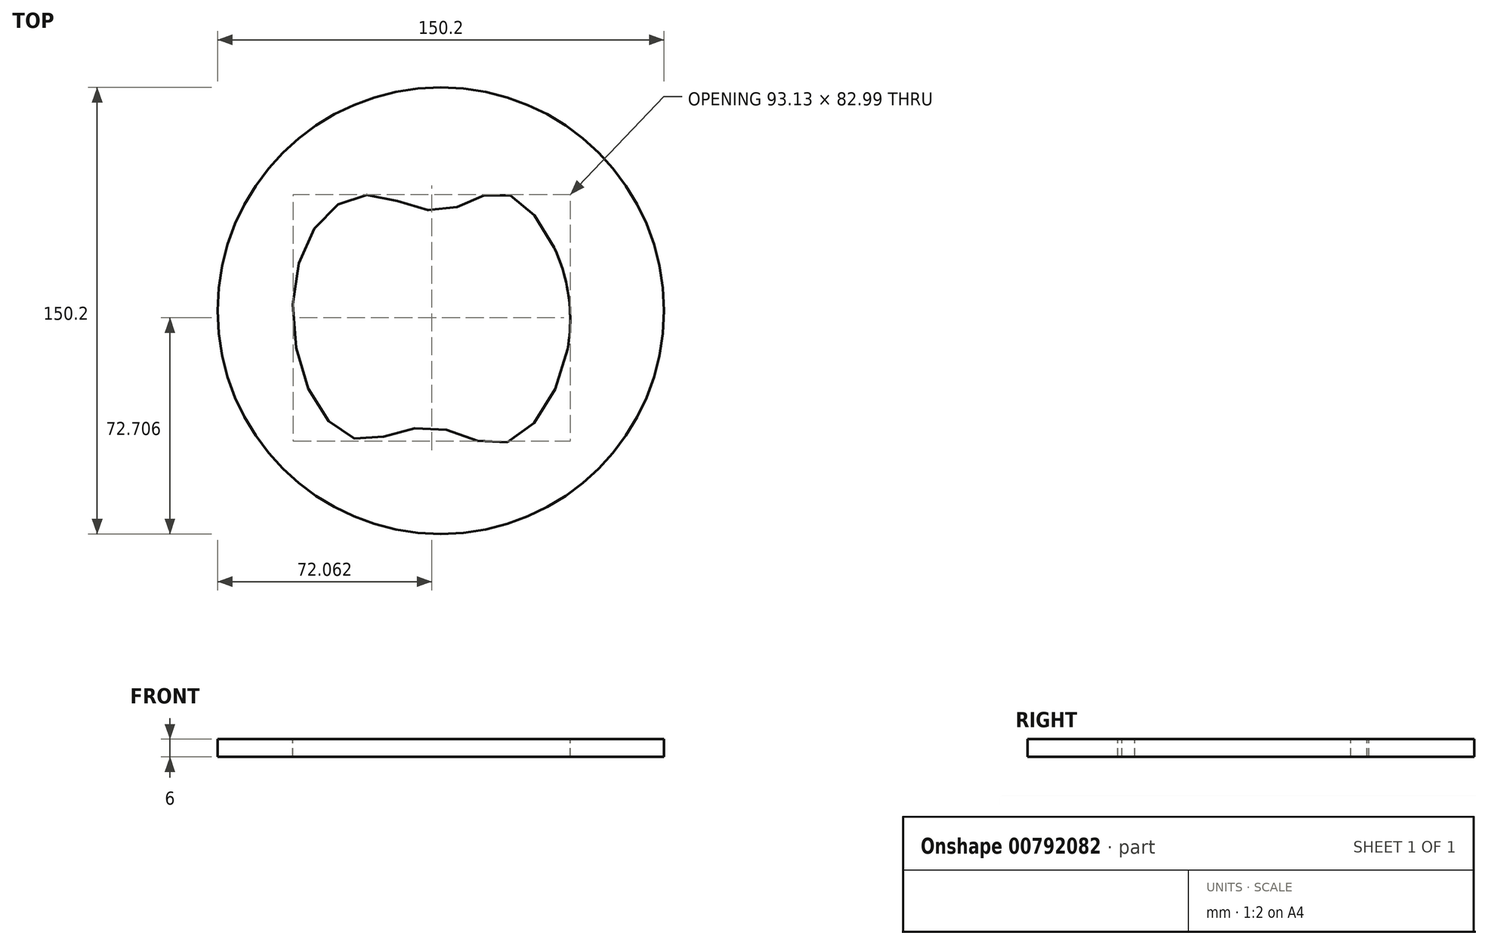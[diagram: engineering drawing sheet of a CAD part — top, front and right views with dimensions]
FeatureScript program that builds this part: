
annotation { "Feature Type Name" : "Feature", "Feature Type Description" : "" }
export const myFeature = defineFeature(function(context is Context, id is Id, definition is map)
    precondition{}
    {
        {
            var Q0;
            Q0=qCreatedBy(makeId("Top.planeOp"),FACE);
            var sketch = newSketch(context, id + "F0", { "sketchPlane" : qUnion([Q0])});
            skFitSpline(sketch, "E0", {"points": [v(0, 33.58) * mm, v(-24.38, 38.97) * mm, v(-44.64, 24) * mm, v(-47.11, -19.07) * mm, v(-28.1, -43.18) * mm, v(-3.62, -39.08) * mm, v(21.1, -44.62) * mm, v(41.5, -17.8) * mm, v(38.38, 20.75) * mm, v(19.93, 39.6) * mm, v(0, 33.58) * mm]});
            skArc(sketch, "E1", {"start": v(38.38, 20.75) * mm, "mid": v(30.12, 2.62) * mm, "end": v(42.63, -12.88) * mm});
            skFitSpline(sketch, "E2", {"points": [v(-9.87, 41.24) * mm, v(0, 52.2) * mm, v(13.38, 54.84) * mm, v(0, 43) * mm, v(-9.87, 41.24) * mm]});
            skFitSpline(sketch, "E3.0", {"points": [v(1.03, 28.65) * mm, v(0.37, 28.6) * mm, v(-0.3, 28.56) * mm, v(-1.18, 28.54) * mm, v(-2.27, 28.57) * mm, v(-3.54, 28.67) * mm, v(-5.2, 28.9) * mm, v(-7.2, 29.31) * mm, v(-9.5, 29.94) * mm, v(-11.73, 30.65) * mm, v(-14.57, 31.63) * mm, v(-17.26, 32.56) * mm, v(-19.75, 33.29) * mm, v(-21.2, 33.62) * mm, v(-22.3, 33.81) * mm, v(-23.1, 33.91) * mm, v(-23.85, 33.97) * mm, v(-24.56, 33.98) * mm, v(-25.27, 33.95) * mm, v(-26.21, 33.85) * mm, v(-27.4, 33.61) * mm, v(-28.81, 33.16) * mm, v(-30.71, 32.31) * mm, v(-33.08, 30.8) * mm, v(-35.8, 28.3) * mm, v(-37.88, 25.68) * mm, v(-39.37, 23.29) * mm, v(-40.4, 21.37) * mm, v(-41.32, 19.32) * mm, v(-42.42, 16.41) * mm, v(-43.52, 12.5) * mm, v(-44.4, 7.46) * mm, v(-44.97, 0.41) * mm, v(-44.61, -6.9) * mm, v(-43.33, -14.04) * mm, v(-41.93, -19.2) * mm, v(-40.09, -24.08) * mm, v(-37.9, -28.48) * mm, v(-35.43, -32.25) * mm, v(-33.25, -34.7) * mm, v(-31.5, -36.2) * mm, v(-30.23, -37.09) * mm, v(-29.21, -37.62) * mm, v(-28.42, -37.94) * mm, v(-27.85, -38.12) * mm, v(-27.38, -38.23) * mm, v(-27.01, -38.3) * mm, v(-26.43, -38.37) * mm, v(-25.5, -38.42) * mm, v(-24.04, -38.3) * mm, v(-22.4, -38.02) * mm, v(-20.61, -37.59) * mm, v(-18.03, -36.85) * mm, v(-15.2, -35.97) * mm, v(-12.16, -35.13) * mm, v(-9.75, -34.58) * mm, v(-7.64, -34.25) * mm, v(-5.9, -34.1) * mm, v(-4.78, -34.06) * mm, v(-3.87, -34.06) * mm, v(-2.95, -34.1) * mm, v(-1.82, -34.2) * mm, v(-0.5, -34.38) * mm, v(1.22, -34.7) * mm, v(3.28, -35.22) * mm, v(5.62, -35.97) * mm, v(7.85, -36.77) * mm, v(10.67, -37.83) * mm, v(13.27, -38.78) * mm, v(15.59, -39.43) * mm, v(17.16, -39.74) * mm, v(18.55, -39.87) * mm, v(19.45, -39.82) * mm, v(20, -39.74) * mm, v(20.37, -39.67) * mm, v(20.84, -39.55) * mm, v(21.44, -39.34) * mm, v(22.26, -39) * mm, v(23.34, -38.38) * mm, v(24.72, -37.38) * mm, v(26.13, -36.12) * mm, v(28.01, -34.1) * mm, v(30.31, -31.04) * mm, v(32.82, -26.68) * mm, v(34.97, -21.9) * mm, v(36.65, -16.9) * mm, v(37.8, -11.93) * mm, v(38.45, -7) * mm, v(38.61, -2.11) * mm, v(38.3, 2.7) * mm, v(37.55, 7.45) * mm, v(36.37, 12.09) * mm, v(35.04, 15.86) * mm, v(33.78, 18.8) * mm, v(32.4, 21.7) * mm, v(30.46, 25.13) * mm, v(27.9, 28.75) * mm, v(25.7, 31.16) * mm, v(23.98, 32.63) * mm, v(22.74, 33.49) * mm, v(21.6, 34.1) * mm, v(20.74, 34.4) * mm, v(20.13, 34.55) * mm, v(19.77, 34.6) * mm, v(19.5, 34.63) * mm, v(19.2, 34.64) * mm, v(18.83, 34.62) * mm, v(18.31, 34.57) * mm, v(17.56, 34.43) * mm, v(16.48, 34.13) * mm, v(15, 33.59) * mm, v(13.36, 32.88) * mm, v(11.57, 32.07) * mm, v(9.65, 31.2) * mm, v(7.6, 30.34) * mm, v(5.74, 29.68) * mm, v(4.18, 29.23) * mm, v(2.96, 28.95) * mm, v(1.9, 28.76) * mm, v(1.03, 28.65) * mm, v(0.37, 28.6) * mm, v(-0.3, 28.56) * mm]});
            skArc(sketch, "E4.0", {"start": v(32.14, 22.1) * mm, "mid": v(25.15, 2.02) * mm, "end": v(36.89, -15.71) * mm});
            skFitSpline(sketch, "E5.0", {"points": [v(-12.34, 39.45) * mm, v(-12.69, 40.14) * mm, v(-12.89, 40.83) * mm, v(-12.96, 41.48) * mm, v(-12.95, 42.08) * mm, v(-12.86, 42.81) * mm, v(-12.63, 43.63) * mm, v(-12.25, 44.53) * mm, v(-11.79, 45.4) * mm, v(-11.24, 46.25) * mm, v(-10.61, 47.1) * mm, v(-9.68, 48.24) * mm, v(-8.34, 49.67) * mm, v(-6.47, 51.37) * mm, v(-4.37, 53) * mm, v(-2.46, 54.27) * mm, v(-0.84, 55.18) * mm, v(0.8, 56.02) * mm, v(2.86, 56.92) * mm, v(5.3, 57.77) * mm, v(7.25, 58.27) * mm, v(8.73, 58.54) * mm, v(9.8, 58.68) * mm, v(10.83, 58.74) * mm, v(11.83, 58.72) * mm, v(12.84, 58.6) * mm, v(13.72, 58.33) * mm, v(14.47, 57.96) * mm, v(15.05, 57.56) * mm, v(15.6, 57) * mm, v(16.05, 56.3) * mm, v(16.35, 55.48) * mm, v(16.45, 54.69) * mm, v(16.41, 53.99) * mm, v(16.25, 53.16) * mm, v(15.92, 52.32) * mm, v(15.42, 51.43) * mm, v(14.84, 50.6) * mm, v(14.17, 49.8) * mm, v(13.43, 49) * mm, v(12.35, 47.93) * mm, v(10.81, 46.58) * mm, v(8.76, 44.95) * mm, v(6.54, 43.38) * mm, v(4.22, 41.9) * mm, v(2.26, 40.78) * mm, v(0.7, 39.98) * mm, v(-0.84, 39.26) * mm, v(-2.7, 38.5) * mm, v(-4.45, 37.95) * mm, v(-5.79, 37.65) * mm, v(-6.76, 37.49) * mm, v(-7.72, 37.4) * mm, v(-8.69, 37.42) * mm, v(-9.7, 37.58) * mm, v(-10.6, 37.92) * mm, v(-11.35, 38.39) * mm, v(-11.88, 38.86) * mm, v(-12.34, 39.45) * mm, v(-12.69, 40.14) * mm, v(-12.89, 40.83) * mm, v(-12.34, 39.45) * mm]});
            skCircle(sketch, "E6", {"center": v(0, 0) * mm, "radius": 75.1 * mm});
            skLineSegment(sketch, "E7", {"start": v(38.11, 21.32) * mm, "end": v(38.38, 20.75) * mm});
            skSolve(sketch);
        }
        {
            var Q0;
            Q0 = qSketchRegion(id + "F0", true);
            var Q1;
            Q1=makeQuery(id+"F0.imprint","IMPRINT",FACE,{"disambiguationData":[TD([[makeQuery(id+"F0.imprint","IMPRINT",EDGE,{"derivedFrom":sQuery(id+"F0.wireOp",EDGE,"E2")}),-1.0]])]});
            var Q2;
            Q2=makeQuery(id+"F0.imprint","IMPRINT",FACE,{"disambiguationData":[TD([[makeQuery(id+"F0.imprint","IMPRINT",EDGE,{"derivedFrom":sQuery(id+"F0.wireOp",EDGE,"E3.0")}),1.0]])]});
            extrude(context, id + "F1", {"entities" : qUnion([Q0, Q1, Q2]), "depth" : 6 * mm, "offsetDistance" : 25 * mm});
        }
    });
